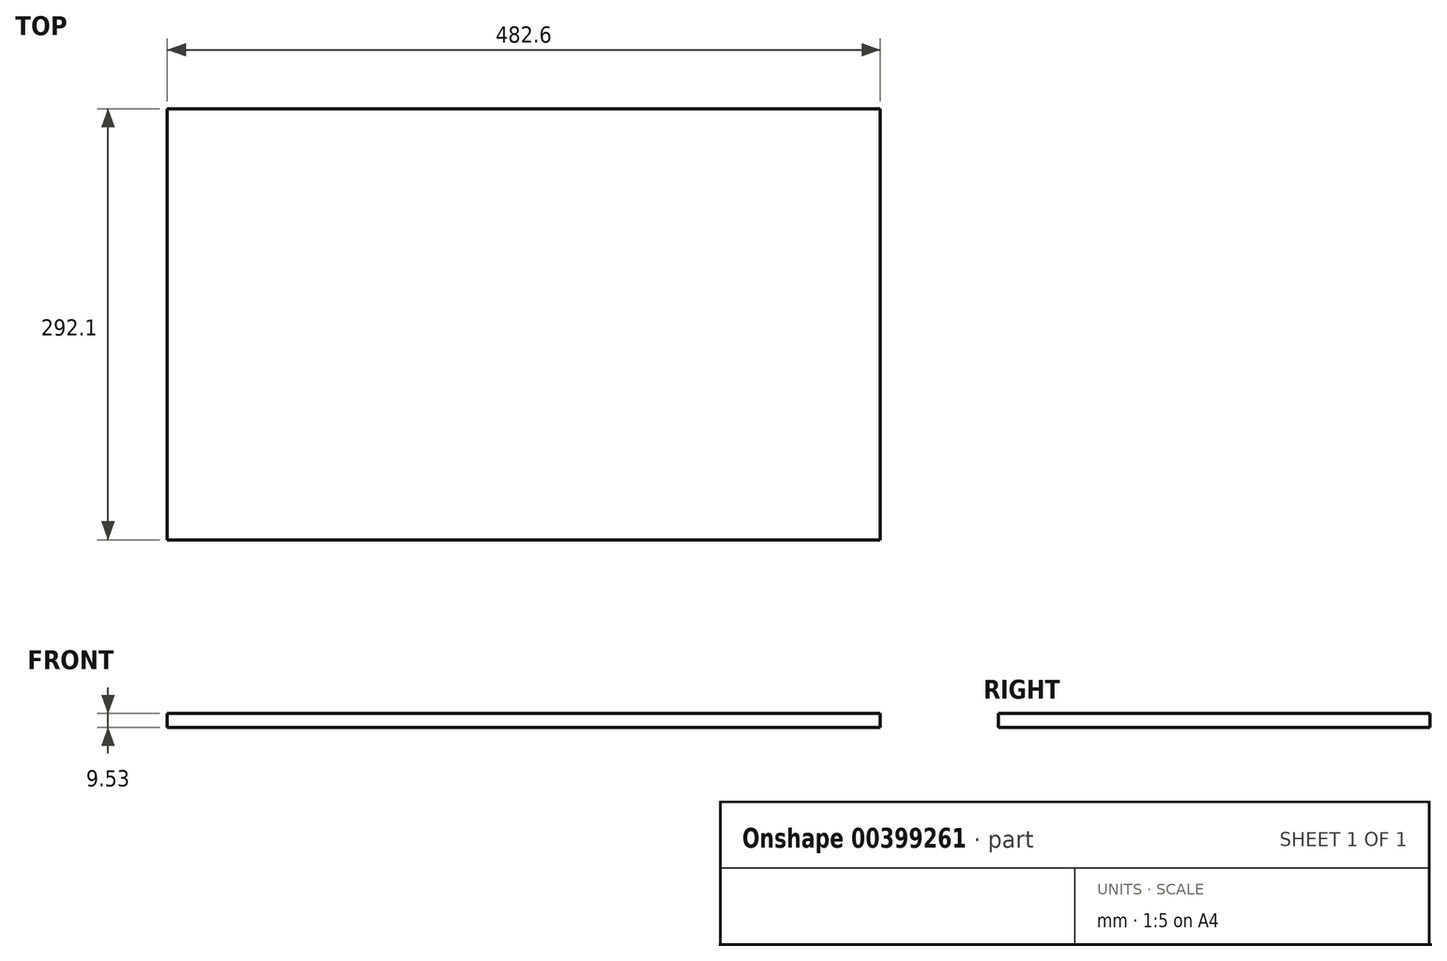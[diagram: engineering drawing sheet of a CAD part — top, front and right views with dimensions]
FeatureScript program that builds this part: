
annotation { "Feature Type Name" : "Feature", "Feature Type Description" : "" }
export const myFeature = defineFeature(function(context is Context, id is Id, definition is map)
    precondition{}
    {
        {
            var Q0;
            Q0=qCreatedBy(makeId("Top.planeOp"),FACE);
            var sketch = newSketch(context, id + "F0", { "sketchPlane" : qUnion([Q0])});
            skLineSegment(sketch, "E0.bottom", {"start": v(0, 0) * mm, "end": v(482.6, 0) * mm});
            skLineSegment(sketch, "E0.top", {"start": v(0, -292.1) * mm, "end": v(482.6, -292.1) * mm});
            skLineSegment(sketch, "E0.left", {"start": v(0, 0) * mm, "end": v(0, -292.1) * mm});
            skLineSegment(sketch, "E0.right", {"start": v(482.6, 0) * mm, "end": v(482.6, -292.1) * mm});
            skSolve(sketch);
        }
        {
            var Q0;
            Q0 = qSketchRegion(id + "F0", true);
            extrude(context, id + "F1", {"entities" : qUnion([Q0]), "depth" : 9.52 * mm});
        }
    });
